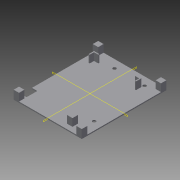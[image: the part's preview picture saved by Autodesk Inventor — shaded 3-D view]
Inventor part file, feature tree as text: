
AUTODESK INVENTOR PART (.ipt)
format: ipt  version: 2015 SP2 (Build 190223200, 223)  size: 169,984 bytes
history: native  units: in
note: dims shown in document units (in); Inventor stores cm internally (conversion verified against a paired STEP export)
features: extrude x4, mirror x4, sketch x4, plane x2, hole x1, projected_geometry x1
ambient origin geometry x8: Origin, YZ Plane, XZ Plane, XY Plane, X Axis, Y Axis, Z Axis, Center Point
bodies: Solid3 (feature_tree)
feature tree (16):
  extrude  "Extrusion4"  Depth=2.1in
  extrude  "Extrusion5"  Depth=0.1181in
  plane  "Work Plane2"
  mirror  "Mirror2"
  plane  "Work Plane3"
  mirror  "Mirror3"
  hole  "Hole1"  [1 undecoded]
  mirror  "Mirror8"
  mirror  "Mirror9"
  extrude  "Extrusion8"  Depth=3.0937in
  extrude  "Extrusion9"  Depth=3.0937in
  sketch  "Sketch1"  dims[d0=2.7in d1=2.1in]
  sketch  "Sketch5"  dims[d2=0.1016in d3=0.1181in]
  sketch  "Sketch7"  dims[d4=0.3in d5=0.1181in]
  projected_geometry  "Projected Loop2"
  sketch  "Sketch8"  dims[d6=1.4in d8=0.1181in d9=0.5512in d10=0.0984in d26=0.0394in d27=0.0in d32=0.2756in d33=0.0in d34=1.6535in d35=2.4409in d39=0.0394in d40=0.1969in d41=0.1969in d44=0.1969in d45=0.1969in d46=0.1969in d47=-1.2469in d48=-1.5469in d49=0.1969in d50=0.1969in d53=0.1969in d54=0.0787in d55=0.1181in d56=0.2362in d57=0.1575in d58=0.0787in d59=90.0deg d60=0.315in d61=0.8108in d62=0.1969in d63=0.1969in d64=0.1969in d65=0.1969in d66=0.2756in d67=0.0in d68=0.1969in d69=0.3937in d70=0.0787in d71=0.0394in d72=0.0in d73=2.4937in d74=3.0937in]
note: 1 required parameter value undecoded (feature->parameter linkage not recoverable at this tier; creation-order binding heuristic only, values carry confidence <= 0.55)
